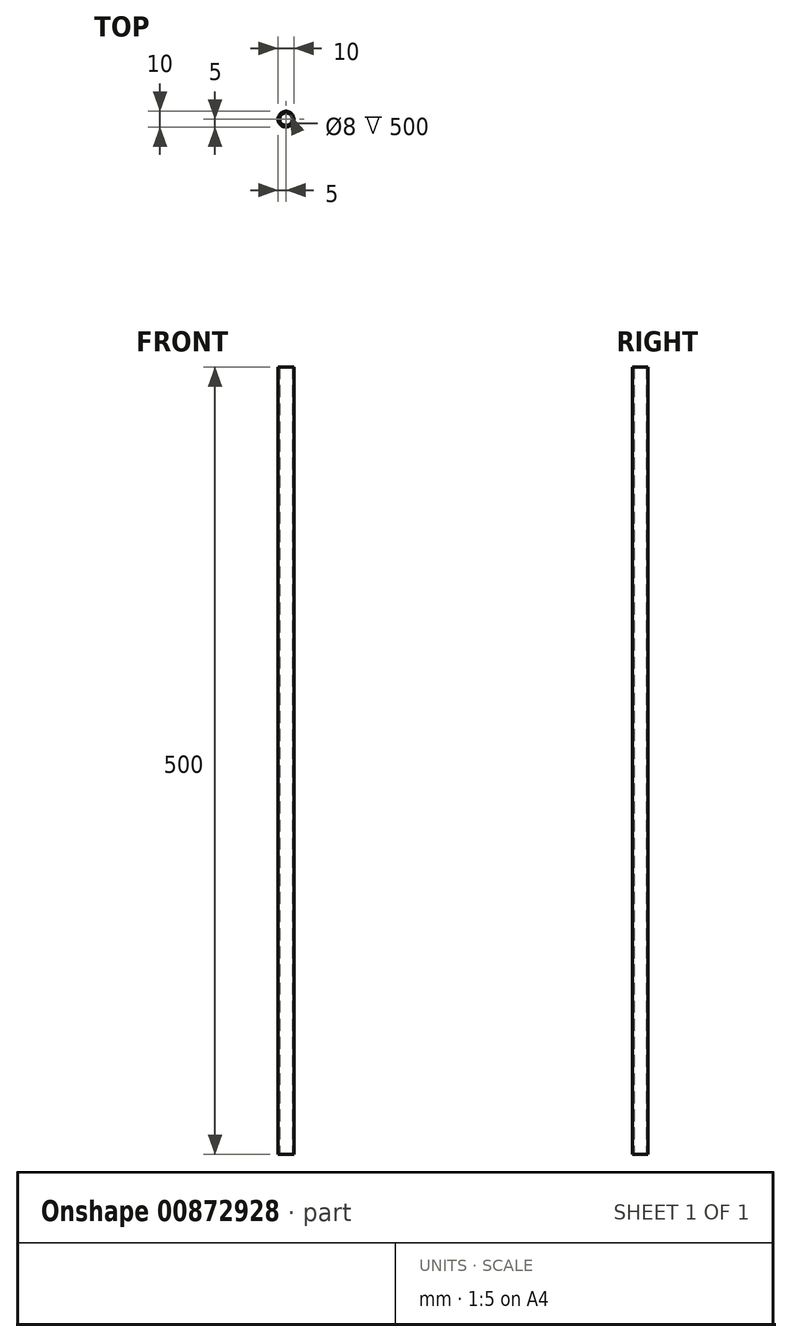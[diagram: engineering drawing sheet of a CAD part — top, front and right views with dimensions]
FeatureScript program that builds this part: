
annotation { "Feature Type Name" : "Feature", "Feature Type Description" : "" }
export const myFeature = defineFeature(function(context is Context, id is Id, definition is map)
    precondition{}
    {
        {
            var Q0;
            Q0=qCreatedBy(makeId("Top.planeOp"),FACE);
            var sketch = newSketch(context, id + "F0", { "sketchPlane" : qUnion([Q0])});
            skCircle(sketch, "E0", {"center": v(0, 0) * mm, "radius": 4 * mm});
            skCircle(sketch, "E1", {"center": v(0, 0) * mm, "radius": 5 * mm});
            skSolve(sketch);
        }
        {
            var Q0;
            Q0=qSketchRegion(id+"F0",true);
            extrude(context, id + "F1", {"entities" : qUnion([Q0]), "endBound" : BoundingType.SYMMETRIC, "depth" : 500 * mm, "offsetDistance" : 25 * mm});
        }
    });
